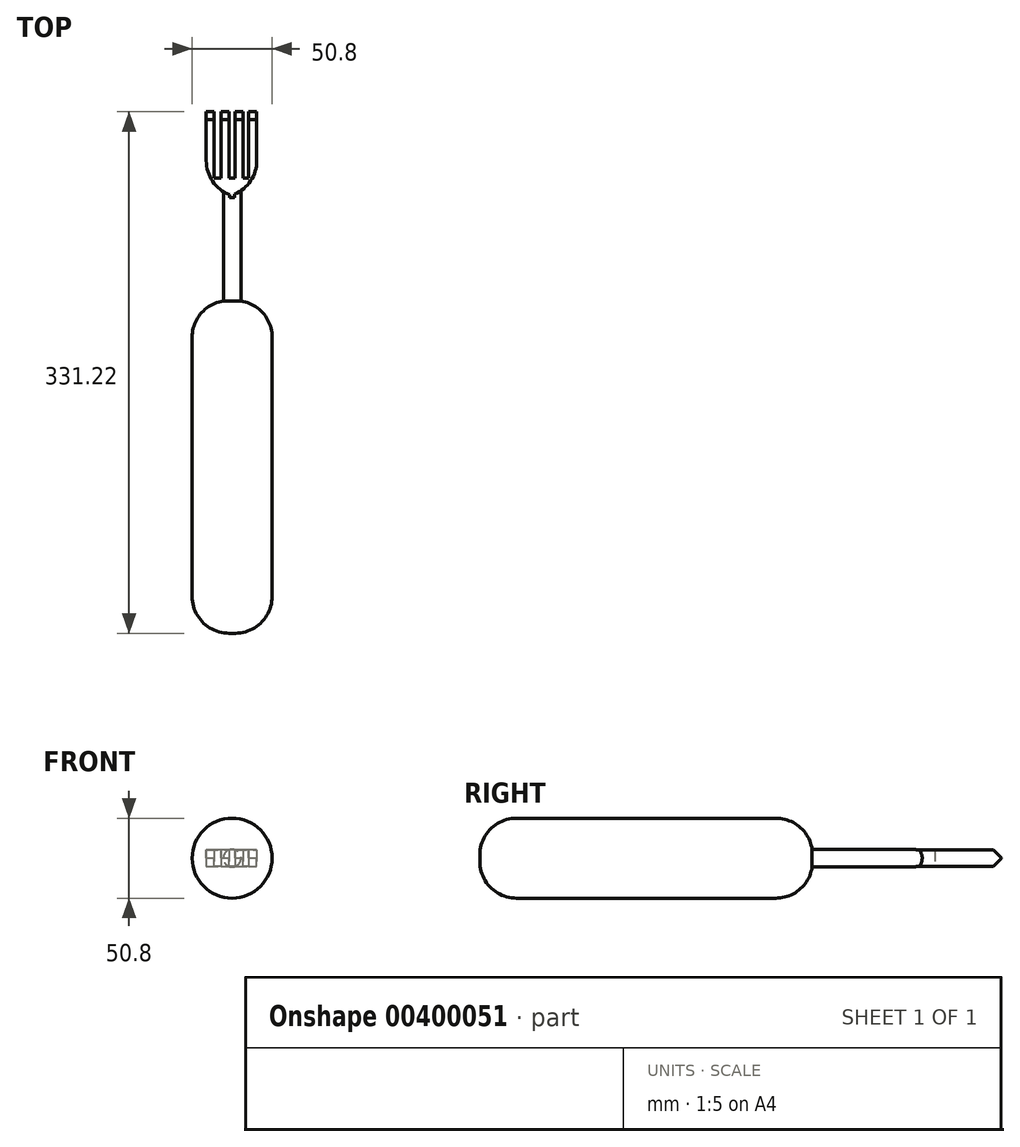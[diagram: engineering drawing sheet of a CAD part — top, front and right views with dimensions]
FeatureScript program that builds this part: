
annotation { "Feature Type Name" : "Feature", "Feature Type Description" : "" }
export const myFeature = defineFeature(function(context is Context, id is Id, definition is map)
    precondition{}
    {
        {
            var Q0;
            Q0=qCreatedBy(makeId("Front.planeOp"),FACE);
            var sketch = newSketch(context, id + "F0", { "sketchPlane" : qUnion([Q0])});
            skCircle(sketch, "E0", {"center": v(0, 0) * mm, "radius": 25.4 * mm});
            skSolve(sketch);
        }
        {
            var Q0;
            Q0=makeQuery(id+"F0.imprint","IMPRINT",FACE,{"disambiguationData":[TD([[makeQuery(id+"F0.imprint","IMPRINT",EDGE,{"derivedFrom":sQuery(id+"F0.wireOp",EDGE,"E0")}),1.0]])]});
            extrude(context, id + "F1", {"entities" : qUnion([Q0]), "oppositeDirection" : true, "depth" : 211.07 * mm});
        }
        {
            var Q0;
            Q0=makeQuery(id+"F1.opExtrude","CAP_FACE",FACE,{"disambiguationData":[OSD([sQuery(id+"F0.wireOp",EDGE,"E0")])],"isStart":false});
            var sketch = newSketch(context, id + "F2", { "sketchPlane" : qUnion([Q0])});
            skCircle(sketch, "E1", {"center": v(0, 0) * mm, "radius": 5.58 * mm});
            skSolve(sketch);
        }
        {
            var Q0;
            Q0 = qSketchRegion(id + "F2", true);
            extrude(context, id + "F3", {"entities" : qUnion([Q0]), "operationType" : NewBodyOperationType.ADD, "depth" : 65.8 * mm});
        }
        {
            var Q0;
            Q0=makeQuery(id+"F3.opExtrude","CAP_FACE",FACE,{"disambiguationData":[OSD([sQuery(id+"F2.wireOp",EDGE,"E1")])],"isStart":false});
            var sketch = newSketch(context, id + "F4", { "sketchPlane" : qUnion([Q0])});
            skLineSegment(sketch, "E2.bottom", {"start": v(-15.63, 5.33) * mm, "end": v(16.42, 5.33) * mm});
            skLineSegment(sketch, "E2.top", {"start": v(-15.63, -5.21) * mm, "end": v(16.42, -5.21) * mm});
            skLineSegment(sketch, "E2.left", {"start": v(-15.63, 5.33) * mm, "end": v(-15.63, -5.21) * mm});
            skLineSegment(sketch, "E2.right", {"start": v(16.42, 5.33) * mm, "end": v(16.42, -5.21) * mm});
            skSolve(sketch);
        }
        {
            var Q0;
            Q0 = qSketchRegion(id + "F4", true);
            extrude(context, id + "F5", {"entities" : qUnion([Q0]), "operationType" : NewBodyOperationType.ADD, "depth" : 12.2 * mm});
        }
        {
            var Q0;
            Q0=makeQuery(id+"F5.opExtrude","CAP_FACE",FACE,{"disambiguationData":[OSD([sQuery(id+"F4.wireOp",EDGE,"E2.bottom"),sQuery(id+"F4.wireOp",EDGE,"E2.top"),sQuery(id+"F4.wireOp",EDGE,"E2.left"),sQuery(id+"F4.wireOp",EDGE,"E2.right")])],"isStart":false});
            var sketch = newSketch(context, id + "F6", { "sketchPlane" : qUnion([Q0])});
            skLineSegment(sketch, "E3.bottom", {"start": v(-15.63, 5.33) * mm, "end": v(-10.55, 5.33) * mm});
            skLineSegment(sketch, "E3.top", {"start": v(-15.63, -5.21) * mm, "end": v(-10.55, -5.21) * mm});
            skLineSegment(sketch, "E3.left", {"start": v(-15.63, 5.33) * mm, "end": v(-15.63, -5.21) * mm});
            skLineSegment(sketch, "E3.right", {"start": v(-10.55, 5.33) * mm, "end": v(-10.55, -5.21) * mm});
            skLineSegment(sketch, "E4.bottom", {"start": v(-6.85, 5.33) * mm, "end": v(-1.77, 5.33) * mm});
            skLineSegment(sketch, "E4.top", {"start": v(-6.85, -5.21) * mm, "end": v(-1.77, -5.21) * mm});
            skLineSegment(sketch, "E4.left", {"start": v(-6.85, 5.33) * mm, "end": v(-6.85, -5.21) * mm});
            skLineSegment(sketch, "E4.right", {"start": v(-1.77, 5.33) * mm, "end": v(-1.77, -5.21) * mm});
            skLineSegment(sketch, "E5.bottom", {"start": v(1.79, 5.33) * mm, "end": v(6.87, 5.33) * mm});
            skLineSegment(sketch, "E5.top", {"start": v(1.79, -5.21) * mm, "end": v(6.87, -5.21) * mm});
            skLineSegment(sketch, "E5.left", {"start": v(1.79, 5.33) * mm, "end": v(1.79, -5.21) * mm});
            skLineSegment(sketch, "E5.right", {"start": v(6.87, 5.33) * mm, "end": v(6.87, -5.21) * mm});
            skLineSegment(sketch, "E6.bottom", {"start": v(16.42, 5.33) * mm, "end": v(11.34, 5.33) * mm});
            skLineSegment(sketch, "E6.top", {"start": v(16.42, -5.21) * mm, "end": v(11.34, -5.21) * mm});
            skLineSegment(sketch, "E6.left", {"start": v(16.42, 5.33) * mm, "end": v(16.42, -5.21) * mm});
            skLineSegment(sketch, "E6.right", {"start": v(11.34, 5.33) * mm, "end": v(11.34, -5.21) * mm});
            skSolve(sketch);
        }
        {
            var Q0;
            Q0 = qSketchRegion(id + "F6", true);
            extrude(context, id + "F7", {"entities" : qUnion([Q0]), "operationType" : NewBodyOperationType.ADD, "depth" : 42.16 * mm});
        }
        {
            var Q0;
            Q0=makeQuery(id+"F7.opExtrude","CAP_EDGE",EDGE,{"disambiguationData":[OSD([sQuery(id+"F6.wireOp",EDGE,"E6.bottom")])],"isStart":false});
            var Q1;
            Q1=makeQuery(id+"F7.opExtrude","CAP_EDGE",EDGE,{"disambiguationData":[OSD([sQuery(id+"F6.wireOp",EDGE,"E6.top")])],"isStart":false});
            var Q2;
            Q2=makeQuery(id+"F7.opExtrude","CAP_EDGE",EDGE,{"disambiguationData":[OSD([sQuery(id+"F6.wireOp",EDGE,"E5.bottom")])],"isStart":false});
            var Q3;
            Q3=makeQuery(id+"F7.opExtrude","CAP_EDGE",EDGE,{"disambiguationData":[OSD([sQuery(id+"F6.wireOp",EDGE,"E5.top")])],"isStart":false});
            var Q4;
            Q4=makeQuery(id+"F7.opExtrude","CAP_EDGE",EDGE,{"disambiguationData":[OSD([sQuery(id+"F6.wireOp",EDGE,"E4.bottom")])],"isStart":false});
            var Q5;
            Q5=makeQuery(id+"F7.opExtrude","CAP_EDGE",EDGE,{"disambiguationData":[OSD([sQuery(id+"F6.wireOp",EDGE,"E4.top")])],"isStart":false});
            var Q6;
            Q6=makeQuery(id+"F7.opExtrude","CAP_EDGE",EDGE,{"disambiguationData":[OSD([sQuery(id+"F6.wireOp",EDGE,"E3.bottom")])],"isStart":false});
            var Q7;
            Q7=makeQuery(id+"F7.opExtrude","CAP_EDGE",EDGE,{"disambiguationData":[OSD([sQuery(id+"F6.wireOp",EDGE,"E3.top")])],"isStart":false});
            chamfer(context, id + "F8", {"entities" : qUnion([Q0, Q1, Q2, Q3, Q4, Q5, Q6, Q7]), "width" : 5.08 * mm, "tangentPropagation" : true});
        }
        {
            var Q0;
            Q0=makeQuery(id+"F5.opExtrude","CAP_EDGE",EDGE,{"disambiguationData":[OSD([sQuery(id+"F4.wireOp",EDGE,"E2.right")])],"isStart":true});
            var Q1;
            Q1=makeQuery(id+"F5.opExtrude","CAP_EDGE",EDGE,{"disambiguationData":[OSD([sQuery(id+"F4.wireOp",EDGE,"E2.left")])],"isStart":true});
            var Q2;
            Q2=makeQuery(id+"F1.opExtrude","CAP_EDGE",EDGE,{"disambiguationData":[OSD([sQuery(id+"F0.wireOp",EDGE,"E0")])],"isStart":false});
            var Q3;
            Q3=makeQuery(id+"F1.opExtrude","CAP_EDGE",EDGE,{"disambiguationData":[OSD([sQuery(id+"F0.wireOp",EDGE,"E0")])],"isStart":true});
            fillet(context, id + "F9", {"entities" : qUnion([Q0, Q1, Q2, Q3]), "radius" : 23.3 * mm, "tangentPropagation" : true, "allowEdgeOverflow" : false});
        }
    });
